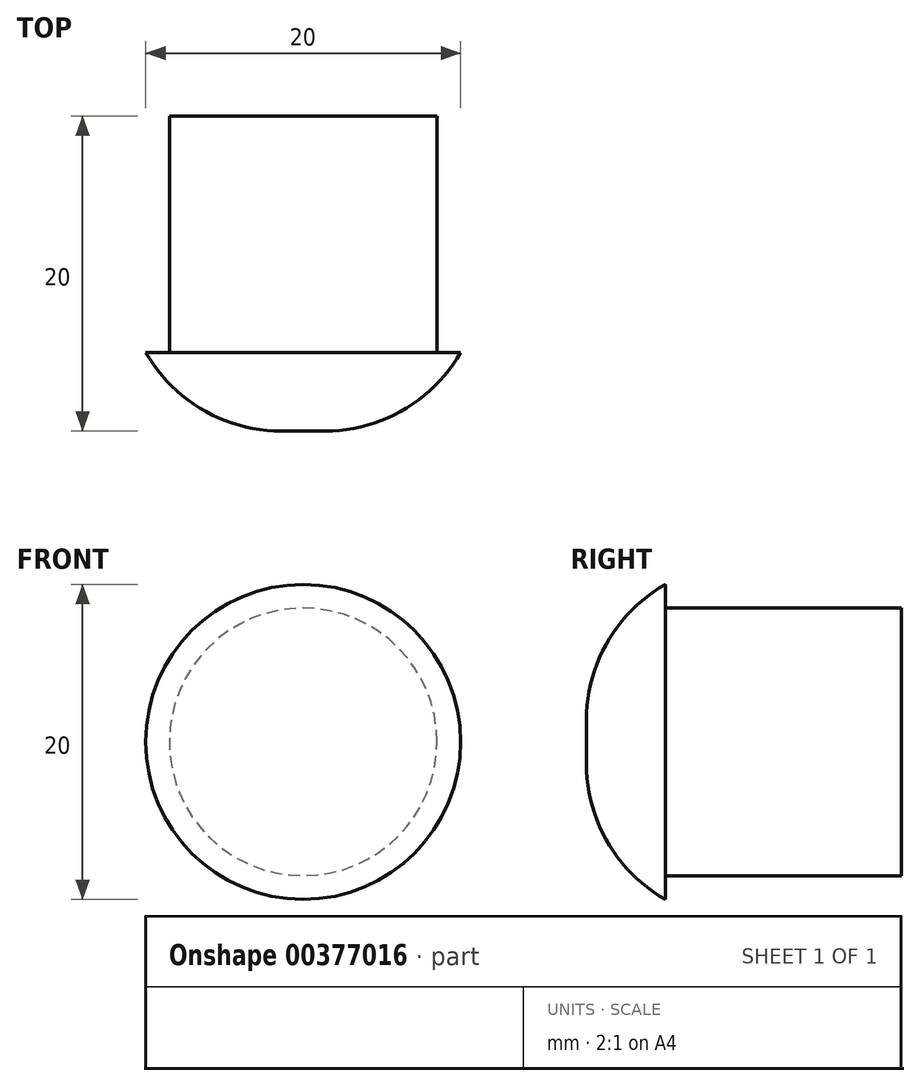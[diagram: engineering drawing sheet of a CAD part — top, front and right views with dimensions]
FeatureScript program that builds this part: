
annotation { "Feature Type Name" : "Feature", "Feature Type Description" : "" }
export const myFeature = defineFeature(function(context is Context, id is Id, definition is map)
    precondition{}
    {
        {
            var Q0;
            Q0=qCreatedBy(makeId("Front.planeOp"),FACE);
            var sketch = newSketch(context, id + "F0", { "sketchPlane" : qUnion([Q0])});
            skCircle(sketch, "E0", {"center": v(0, 0) * mm, "radius": 8.5 * mm});
            skSolve(sketch);
        }
        {
            var Q0;
            Q0=qSketchRegion(id+"F0",true);
            extrude(context, id + "F1", {"entities" : qUnion([Q0]), "depth" : 15 * mm});
        }
        {
            var Q0;
            Q0=makeQuery(id+"F1.opExtrude","CAP_FACE",FACE,{"disambiguationData":[OSD([sQuery(id+"F0.wireOp",EDGE,"E0")])],"isStart":false});
            var sketch = newSketch(context, id + "F2", { "sketchPlane" : qUnion([Q0])});
            skCircle(sketch, "E1", {"center": v(0, 0) * mm, "radius": 10 * mm});
            skSolve(sketch);
        }
        {
            var Q0;
            Q0=qSketchRegion(id+"F2",true);
            extrude(context, id + "F3", {"entities" : qUnion([Q0]), "operationType" : NewBodyOperationType.ADD, "depth" : 5 * mm});
        }
        {
            var Q0;
            Q0=makeQuery(id+"F3.opExtrude","CAP_EDGE",EDGE,{"disambiguationData":[OSD([sQuery(id+"F2.wireOp",EDGE,"E1")])],"isStart":false});
            fillet(context, id + "F4", {"entities" : qUnion([Q0]), "radius" : 9.9 * mm, "allowEdgeOverflow" : false});
        }
    });
